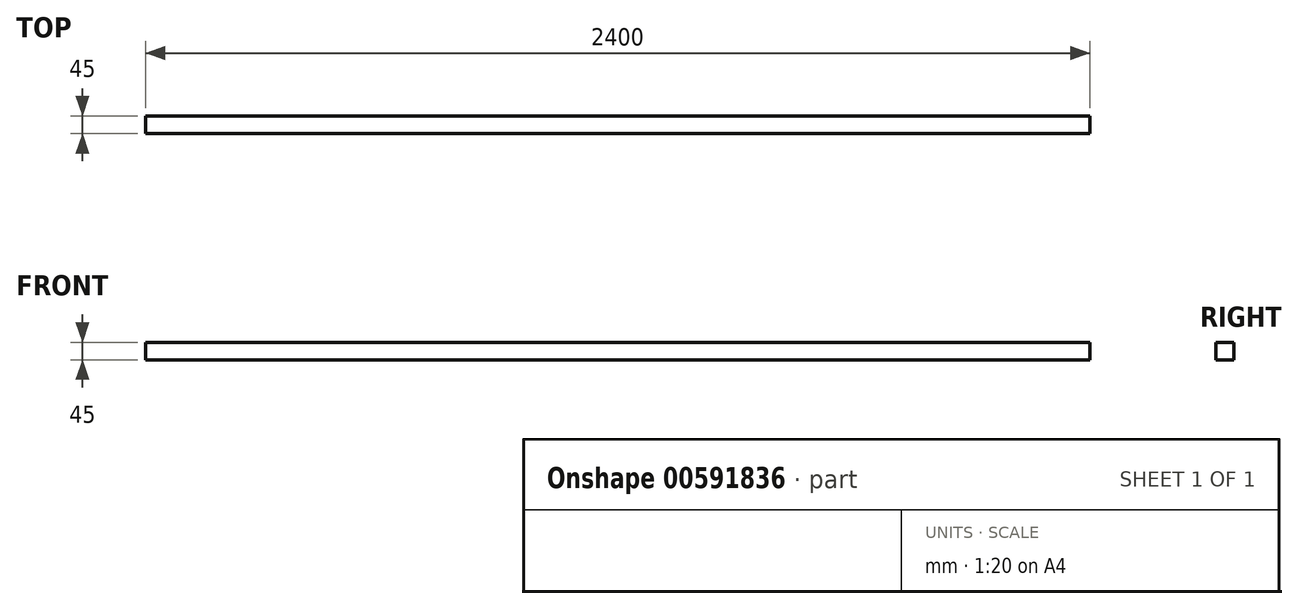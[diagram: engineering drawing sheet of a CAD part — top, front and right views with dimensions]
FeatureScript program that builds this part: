
annotation { "Feature Type Name" : "Feature", "Feature Type Description" : "" }
export const myFeature = defineFeature(function(context is Context, id is Id, definition is map)
    precondition{}
    {
        {
            var Q0;
            Q0=qCreatedBy(makeId("Right.planeOp"),FACE);
            var sketch = newSketch(context, id + "F0", { "sketchPlane" : qUnion([Q0])});
            skLineSegment(sketch, "E0.bottom", {"start": v(0, 0) * mm, "end": v(45, 0) * mm});
            skLineSegment(sketch, "E0.top", {"start": v(0, 45) * mm, "end": v(45, 45) * mm});
            skLineSegment(sketch, "E0.left", {"start": v(0, 0) * mm, "end": v(0, 45) * mm});
            skLineSegment(sketch, "E0.right", {"start": v(45, 0) * mm, "end": v(45, 45) * mm});
            skSolve(sketch);
        }
        {
            var Q0;
            Q0=makeQuery(id+"F0.imprint","IMPRINT",FACE,{"disambiguationData":[TD([[makeQuery(id+"F0.imprint","IMPRINT",EDGE,{"derivedFrom":sQuery(id+"F0.wireOp",EDGE,"E0.bottom")}),1.0]])]});
            extrude(context, id + "F1", {"entities" : qUnion([Q0]), "depth" : 2400 * mm, "offsetDistance" : 25 * mm});
        }
    });
